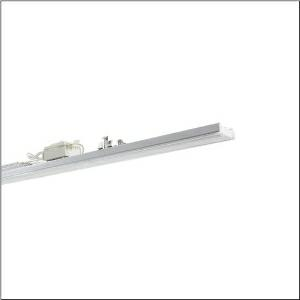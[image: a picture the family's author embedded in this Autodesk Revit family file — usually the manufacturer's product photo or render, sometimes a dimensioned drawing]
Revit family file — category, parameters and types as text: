
# Revit family: licross_r__11_recessed_mo_51tl14dn49xg_a7fc
name_source: partatom
category: Lighting Fixtures
units: mm (PartAtom-declared; Revit-internal decimal feet)

## family parameters
Cut with Voids When Loaded = No
Host = Face
Light Source = No
Part Type = Normal
Room Calculation Point = No
Round Connector Dimension = Use Diameter
Shared = No

## types (1)
- --- (1 x LED, 9430 lm, 56.7 W, 4000K)
    Apparent Load = 57 VA
    CIE Flux Codes = 56 84 97 100 100
    Color Rendering = 80
    Color Temperature = 4000K
    Default Elevation = 1800 mm
    Description = Licross® 11 Recessed MO, luminaire insert, of sheet steel, coil coated, white, length: 1.500mm, width: 66mm, height: 67mm, LED rated luminous flux: 9.430lm, light colour: 840, control gear: DALI 2, with plug, 5-pole, with phase selection, mains connection: 220..240V, AC, 50/60Hz, rated input power: 57W, internal wiring halogen-free, primary light control with lens, of plastic, primary optical cover: cover, of PMMA, light emission: direct distribution, primary light characteristic: asymmetric, protection rating (complete): IP40, insulation class (complete): insulation class I (protective earthing), certification: CE, ENEC, VDE, UKCA, protection symbol: D if used in an environment without relevant dust loads with corresponding accessories, impact resistance: IK06, permissible ambient temperature for indoor applications: -25..+35°C, corresponds to IFS (International Featured Standards) requirements for safety and quality in the food industry, reducing of maximum allowable ambient temperature of 5°C with ceiling mounting, LABS conformity tested according to VDMA 24364:2018-05, packaging unit: 1 piece
    Height = 58 mm
    Lamp = 1 x LED
    Lamp Light Flux = 9430 lm
    Lamp Power = 56.7 W
    Lamp count = 1
    Length = 1500 mm
    Luminous efficacy = 166 lm/W
    Manufacturer = Siteco
    ModVariant = No
    Model = 51TL14DN49XG
    Mounting Place = Ceiling
    Mounting Type = Pendant
    Number of Poles = 1
    OnlyDefault = Yes
    Power Factor = 1
    Product Name = Licross® 11 Recessed MO
    Product group = luminaire insert | ceiling pendant
    ProductGroupID = 902
    Protection Class = Protection class I
    Protection Degree = IP 40
    RLX_Detail_Level = 1
    RLX_Emergency_Light_Flux = 0 lm
    RLX_Emergency_Type = 0
    RLX_Emergency_Type_DB = No
    RlxData = <blob elided: 24965 chars, md5=397165bb>
    Socket = socket
    Standby Power = 0 W
    System Light Flux = 9430 lm
    System Power = 57 W
    Type Comments = factory setting: luminous flux: 100 % | dim-lin: 254 | 378 mA
    Type Image = l_1296930.jpg
    URL = http://relux.com
    VarID = @adj_121497
    Voltage = 0 V
    Weight = 0.00 kg
    Width = 66 mm

## geometry (parser evidence)
native form markers: Blend x4, Sweep x10
no freeform markers — native parametric forms only
